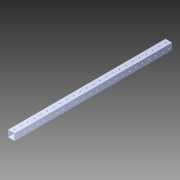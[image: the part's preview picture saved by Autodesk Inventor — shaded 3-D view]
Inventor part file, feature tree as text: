
AUTODESK INVENTOR PART (.ipt)
format: ipt  version: 2014 SP1 (Build 180222100, 222)  size: 1,221,120 bytes
history: native  units: in
note: dims shown in document units (in); Inventor stores cm internally (conversion verified against a paired STEP export)
features: pattern_circular x1, other x1, extrude x1, imported_body x1, sketch x1
ambient origin geometry x8: Origin, YZ Plane, XZ Plane, XY Plane, X Axis, Y Axis, Z Axis, Center Point
bodies: Body1 (feature_tree)
feature tree (5):
  pattern_circular  "CirPattern2"
  other  "1x1 tube1"
  extrude  "Extrusion1"  [1 undecoded]
  imported_body  "Base1"
  sketch  "Sketch1"  dims[d0=35.0in d1=0.0in]
note: 1 required parameter value undecoded (feature->parameter linkage not recoverable at this tier; creation-order binding heuristic only, values carry confidence <= 0.55)
